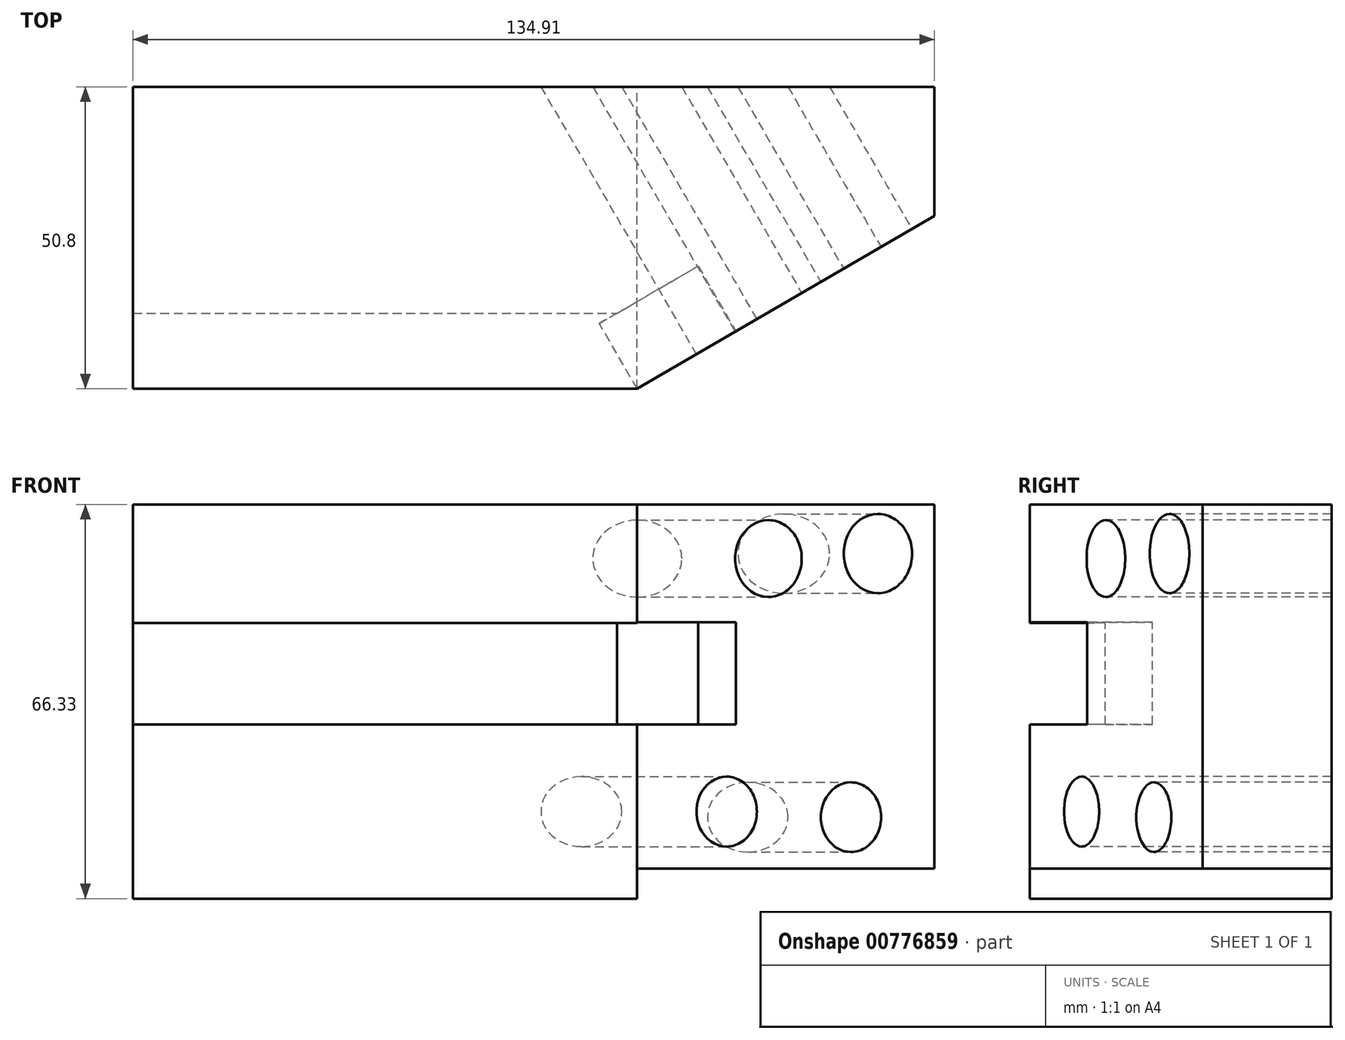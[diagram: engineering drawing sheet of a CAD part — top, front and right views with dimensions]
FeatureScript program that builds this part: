
annotation { "Feature Type Name" : "Feature", "Feature Type Description" : "" }
export const myFeature = defineFeature(function(context is Context, id is Id, definition is map)
    precondition{}
    {
        {
            var Q0;
            Q0=qCreatedBy(makeId("Front.planeOp"),FACE);
            var sketch = newSketch(context, id + "F0", { "sketchPlane" : qUnion([Q0])});
            skLineSegment(sketch, "E0.bottom", {"start": v(-65.2, 37.03) * mm, "end": v(69.7, 37.03) * mm});
            skLineSegment(sketch, "E0.top", {"start": v(-65.2, -29.3) * mm, "end": v(69.7, -29.3) * mm});
            skLineSegment(sketch, "E0.left", {"start": v(-65.2, 37.03) * mm, "end": v(-65.2, -29.3) * mm});
            skLineSegment(sketch, "E0.right", {"start": v(69.7, 37.03) * mm, "end": v(69.7, -29.3) * mm});
            skSolve(sketch);
        }
        {
            var Q0;
            Q0=makeQuery(id+"F0.imprint","IMPRINT",FACE,{"disambiguationData":[TD([[makeQuery(id+"F0.imprint","IMPRINT",EDGE,{"derivedFrom":sQuery(id+"F0.wireOp",EDGE,"E0.bottom")}),-1.0]])]});
            extrude(context, id + "F1", {"entities" : qUnion([Q0]), "depth" : 50.8 * mm, "offsetDistance" : 25.4 * mm});
        }
        {
            var Q0;
            Q0=makeQuery(id+"F1.opExtrude","SWEPT_FACE",FACE,{"disambiguationData":[OSD([sQuery(id+"F0.wireOp",EDGE,"E0.top")])]});
            var sketch = newSketch(context, id + "F2", { "sketchPlane" : qUnion([Q0])});
            skLineSegment(sketch, "E1", {"start": v(-6.83, 66.2) * mm, "end": v(92.72, 8.33) * mm});
            skArc(sketch, "E2", {"start": v(92.72, 8.33) * mm, "mid": v(64.33, 74.06) * mm, "end": v(-6.83, 66.2) * mm});
            skSolve(sketch);
        }
        {
            var Q0;
            {var subQ0=sQuery(id+"F2.wireOp",EDGE,"E1");var subQ1=sQuery(id+"F0.wireOp",EDGE,"E0.top");var subQ2=makeQuery(id+"F1.opExtrude","CAP_EDGE",EDGE,{"disambiguationData":[OSD([subQ1])],"isStart":false});var subQ3=makeQuery(id+"F2.imprint","INTERSECT",VERTEX,{"derivedFrom":[subQ2,subQ0]});Q0=makeQuery(id+"F2.imprint","IMPRINT",FACE,{"disambiguationData":[TD([[makeQuery(id+"F2.imprint","IMPRINT",EDGE,{"disambiguationData":[TD([[subQ3,-1.0]])],"derivedFrom":subQ0}),1.0]])]});}
            extrude(context, id + "F3", {"entities" : qUnion([Q0]), "operationType" : NewBodyOperationType.REMOVE, "endBound" : BoundingType.THROUGH_ALL, "oppositeDirection" : true, "depth" : 25.4 * mm, "offsetDistance" : 25.4 * mm});
        }
        {
            var Q0;
            Q0=makeQuery(id+"F1.opExtrude","CAP_FACE",FACE,{"disambiguationData":[OSD([sQuery(id+"F0.wireOp",EDGE,"E0.bottom"),sQuery(id+"F0.wireOp",EDGE,"E0.top"),sQuery(id+"F0.wireOp",EDGE,"E0.left"),sQuery(id+"F0.wireOp",EDGE,"E0.right")])],"isStart":false});
            var sketch = newSketch(context, id + "F4", { "sketchPlane" : qUnion([Q0])});
            skLineSegment(sketch, "E3.bottom", {"start": v(-65.2, 17.06) * mm, "end": v(19.67, 17.06) * mm});
            skLineSegment(sketch, "E3.top", {"start": v(-65.2, 0) * mm, "end": v(19.67, 0) * mm});
            skLineSegment(sketch, "E3.left", {"start": v(-65.2, 17.06) * mm, "end": v(-65.2, 0) * mm});
            skLineSegment(sketch, "E3.right", {"start": v(19.67, 17.06) * mm, "end": v(19.67, 0) * mm});
            skSolve(sketch);
        }
        {
            var Q0;
            Q0=makeQuery(id+"F4.imprint","IMPRINT",FACE,{"disambiguationData":[TD([[makeQuery(id+"F4.imprint","IMPRINT",EDGE,{"derivedFrom":sQuery(id+"F4.wireOp",EDGE,"E3.bottom")}),-1.0]])]});
            extrude(context, id + "F5", {"entities" : qUnion([Q0]), "operationType" : NewBodyOperationType.REMOVE, "oppositeDirection" : true, "depth" : 12.7 * mm, "offsetDistance" : 25.4 * mm});
        }
        {
            var Q0;
            Q0=makeQuery(id+"F3.boolean.opBoolean","COPY",FACE,{"derivedFrom":makeQuery(id+"F3.opExtrude","SWEPT_FACE",FACE,{"disambiguationData":[OSD([sQuery(id+"F2.wireOp",EDGE,"E1")])]})});
            var sketch = newSketch(context, id + "F6", { "sketchPlane" : qUnion([Q0])});
            skLineSegment(sketch, "E4.bottom", {"start": v(-8.53, 0) * mm, "end": v(10.7, 0) * mm});
            skLineSegment(sketch, "E4.top", {"start": v(-8.53, 17.2) * mm, "end": v(10.7, 17.2) * mm});
            skLineSegment(sketch, "E4.left", {"start": v(-8.53, 0) * mm, "end": v(-8.53, 17.2) * mm});
            skLineSegment(sketch, "E4.right", {"start": v(10.7, 0) * mm, "end": v(10.7, 17.2) * mm});
            skSolve(sketch);
        }
        {
            var Q0;
            {var subQ2=sQuery(id+"F6.wireOp",EDGE,"E4.bottom");Q0=makeQuery(id+"F6.imprint","IMPRINT",FACE,{"disambiguationData":[TD([[makeQuery(id+"F6.imprint","IMPRINT",EDGE,{"derivedFrom":subQ2}),1.0]])]});}
            extrude(context, id + "F7", {"entities" : qUnion([Q0]), "operationType" : NewBodyOperationType.REMOVE, "oppositeDirection" : true, "depth" : 12.7 * mm, "offsetDistance" : 25.4 * mm});
        }
        {
            var Q0;
            Q0=makeQuery(id+"F3.boolean.opBoolean","COPY",FACE,{"derivedFrom":makeQuery(id+"F3.opExtrude","SWEPT_FACE",FACE,{"disambiguationData":[OSD([sQuery(id+"F2.wireOp",EDGE,"E1")])]})});
            var sketch = newSketch(context, id + "F8", { "sketchPlane" : qUnion([Q0])});
            skCircle(sketch, "E5", {"center": v(8.88, -14.65) * mm, "radius": 5.88 * mm});
            skPoint(sketch, "E5.centerSnap0", {"position": v(-8.53, -14.65) * mm});
            skCircle(sketch, "E6", {"center": v(31.4, -14.1) * mm, "radius": 6.7 * mm});
            skCircle(sketch, "E7", {"center": v(15.5, 27.43) * mm, "radius": 6.66 * mm});
            skCircle(sketch, "E8", {"center": v(36.5, 27.89) * mm, "radius": 7.55 * mm});
            skSolve(sketch);
        }
        {
            var Q0;
            Q0=makeQuery(id+"F8.imprint","IMPRINT",FACE,{"disambiguationData":[TD([[makeQuery(id+"F8.imprint","IMPRINT",EDGE,{"derivedFrom":sQuery(id+"F8.wireOp",EDGE,"E5")}),1.0]])]});
            extrude(context, id + "F9", {"entities" : qUnion([Q0]), "operationType" : NewBodyOperationType.REMOVE, "endBound" : BoundingType.THROUGH_ALL, "oppositeDirection" : true, "depth" : 25.4 * mm, "offsetDistance" : 25.4 * mm});
        }
        {
            var Q0;
            Q0=makeQuery(id+"F3.boolean.opBoolean","COPY",FACE,{"derivedFrom":makeQuery(id+"F3.opExtrude","SWEPT_FACE",FACE,{"disambiguationData":[OSD([sQuery(id+"F2.wireOp",EDGE,"E1")])]})});
            var sketch = newSketch(context, id + "F10", { "sketchPlane" : qUnion([Q0])});
            skCircle(sketch, "E9", {"center": v(33.08, -15.6) * mm, "radius": 5.86 * mm});
            skCircle(sketch, "E10", {"center": v(17.01, 27.93) * mm, "radius": 6.48 * mm});
            skCircle(sketch, "E11", {"center": v(38.32, 28.78) * mm, "radius": 6.66 * mm});
            skSolve(sketch);
        }
        {
            var Q0;
            Q0=makeQuery(id+"F10.imprint","IMPRINT",FACE,{"disambiguationData":[TD([[makeQuery(id+"F10.imprint","IMPRINT",EDGE,{"derivedFrom":sQuery(id+"F10.wireOp",EDGE,"E9")}),1.0]])]});
            var Q1;
            Q1=makeQuery(id+"F10.imprint","IMPRINT",FACE,{"disambiguationData":[TD([[makeQuery(id+"F10.imprint","IMPRINT",EDGE,{"derivedFrom":sQuery(id+"F10.wireOp",EDGE,"E10")}),1.0]])]});
            var Q2;
            Q2=makeQuery(id+"F10.imprint","IMPRINT",FACE,{"disambiguationData":[TD([[makeQuery(id+"F10.imprint","IMPRINT",EDGE,{"derivedFrom":sQuery(id+"F10.wireOp",EDGE,"E11")}),1.0]])]});
            extrude(context, id + "F11", {"entities" : qUnion([Q0, Q1, Q2]), "operationType" : NewBodyOperationType.REMOVE, "endBound" : BoundingType.THROUGH_ALL, "oppositeDirection" : true, "depth" : 25.4 * mm, "offsetDistance" : 25.4 * mm});
        }
        {
            var Q0;
            Q0=makeQuery(id+"F1.opExtrude","SWEPT_FACE",FACE,{"disambiguationData":[OSD([sQuery(id+"F0.wireOp",EDGE,"E0.top")])]});
            var sketch = newSketch(context, id + "F12", { "sketchPlane" : qUnion([Q0])});
            skLineSegment(sketch, "E12", {"start": v(19.67, 50.8) * mm, "end": v(19.67, 0) * mm});
            skLineSegment(sketch, "E13", {"start": v(19.67, 50.8) * mm, "end": v(101.12, 3.45) * mm});
            skLineSegment(sketch, "E14", {"start": v(19.67, 0) * mm, "end": v(101.12, 0) * mm});
            skLineSegment(sketch, "E15", {"start": v(100.94, 0.97) * mm, "end": v(101.12, 3.45) * mm});
            skSolve(sketch);
        }
        {
            var Q0;
            {var subQ0=sQuery(id+"F12.wireOp",EDGE,"E12");Q0=makeQuery(id+"F12.imprint","IMPRINT",FACE,{"disambiguationData":[TD([[makeQuery(id+"F12.imprint","IMPRINT",EDGE,{"derivedFrom":subQ0}),1.0]])]});}
            extrude(context, id + "F13", {"entities" : qUnion([Q0]), "operationType" : NewBodyOperationType.REMOVE, "oppositeDirection" : true, "depth" : 5.08 * mm, "offsetDistance" : 25.4 * mm});
        }
    });
